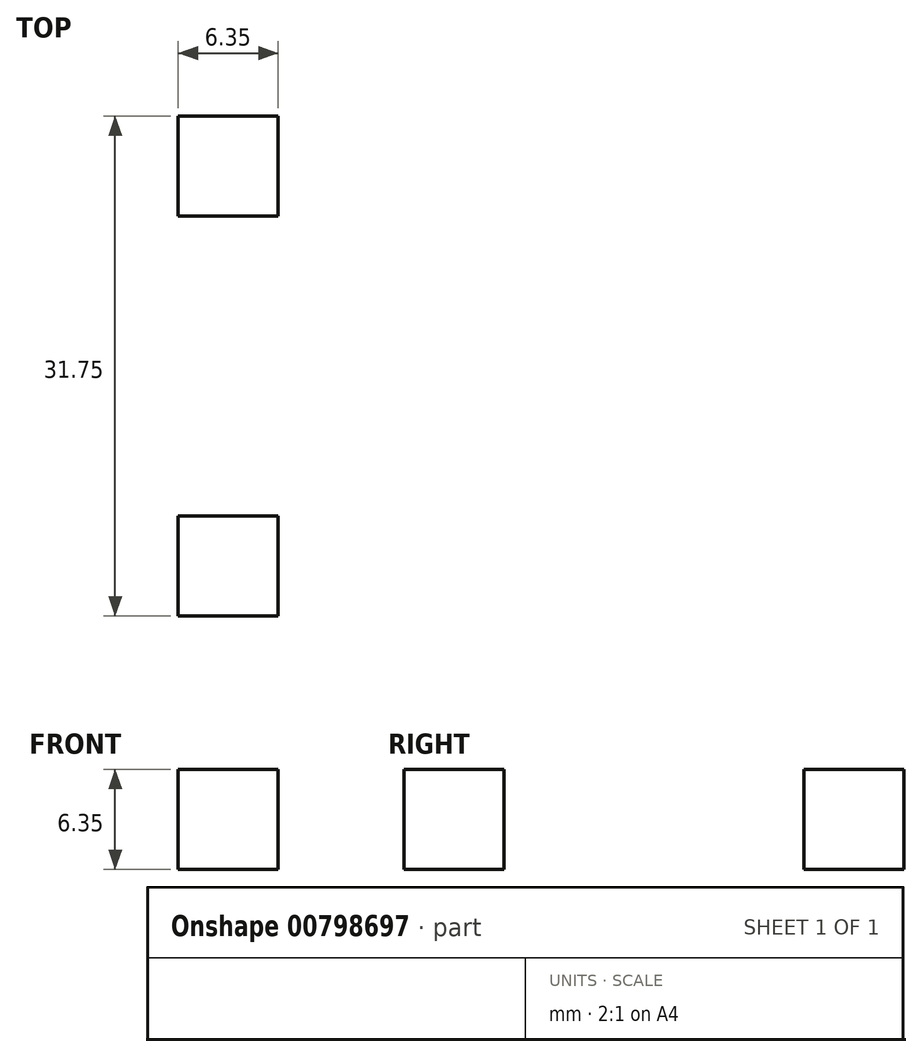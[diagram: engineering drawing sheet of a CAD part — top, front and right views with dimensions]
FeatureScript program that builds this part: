
annotation { "Feature Type Name" : "Feature", "Feature Type Description" : "" }
export const myFeature = defineFeature(function(context is Context, id is Id, definition is map)
    precondition{}
    {
        {
            var Q0;
            Q0=qCreatedBy(makeId("Top.planeOp"),FACE);
            var sketch = newSketch(context, id + "F0", { "sketchPlane" : qUnion([Q0])});
            skLineSegment(sketch, "E0.bottom", {"start": v(0, 0) * mm, "end": v(225.43, 0) * mm});
            skLineSegment(sketch, "E0.top", {"start": v(0, 31.75) * mm, "end": v(225.43, 31.75) * mm});
            skLineSegment(sketch, "E0.left", {"start": v(0, 0) * mm, "end": v(0, 31.75) * mm});
            skLineSegment(sketch, "E0.right", {"start": v(225.43, 0) * mm, "end": v(225.43, 31.75) * mm});
            skLineSegment(sketch, "E1.bottom", {"start": v(0, 31.75) * mm, "end": v(6.35, 31.75) * mm});
            skLineSegment(sketch, "E1.top", {"start": v(0, 25.4) * mm, "end": v(6.35, 25.4) * mm});
            skLineSegment(sketch, "E1.left", {"start": v(0, 31.75) * mm, "end": v(0, 25.4) * mm});
            skLineSegment(sketch, "E1.right", {"start": v(6.35, 31.75) * mm, "end": v(6.35, 25.4) * mm});
            skLineSegment(sketch, "E2.bottom", {"start": v(0, 0) * mm, "end": v(6.35, 0) * mm});
            skLineSegment(sketch, "E2.top", {"start": v(0, 6.35) * mm, "end": v(6.35, 6.35) * mm});
            skLineSegment(sketch, "E2.left", {"start": v(0, 0) * mm, "end": v(0, 6.35) * mm});
            skLineSegment(sketch, "E2.right", {"start": v(6.35, 0) * mm, "end": v(6.35, 6.35) * mm});
            skLineSegment(sketch, "E3.bottom", {"start": v(31.75, 0) * mm, "end": v(38.1, 0) * mm});
            skLineSegment(sketch, "E3.top", {"start": v(31.75, 6.35) * mm, "end": v(38.1, 6.35) * mm});
            skLineSegment(sketch, "E3.left", {"start": v(31.75, 0) * mm, "end": v(31.75, 6.35) * mm});
            skLineSegment(sketch, "E3.right", {"start": v(38.1, 0) * mm, "end": v(38.1, 6.35) * mm});
            skLineSegment(sketch, "E4.bottom", {"start": v(31.75, 25.4) * mm, "end": v(38.1, 25.4) * mm});
            skLineSegment(sketch, "E4.top", {"start": v(31.75, 31.75) * mm, "end": v(38.1, 31.75) * mm});
            skLineSegment(sketch, "E4.left", {"start": v(31.75, 25.4) * mm, "end": v(31.75, 31.75) * mm});
            skLineSegment(sketch, "E4.right", {"start": v(38.1, 25.4) * mm, "end": v(38.1, 31.75) * mm});
            skLineSegment(sketch, "E5.bottom", {"start": v(219.08, 6.35) * mm, "end": v(225.43, 6.35) * mm});
            skLineSegment(sketch, "E5.top", {"start": v(219.08, 0) * mm, "end": v(225.43, 0) * mm});
            skLineSegment(sketch, "E5.left", {"start": v(219.08, 6.35) * mm, "end": v(219.08, 0) * mm});
            skLineSegment(sketch, "E5.right", {"start": v(225.43, 6.35) * mm, "end": v(225.43, 0) * mm});
            skLineSegment(sketch, "E6.bottom", {"start": v(219.08, 25.4) * mm, "end": v(225.43, 25.4) * mm});
            skLineSegment(sketch, "E6.top", {"start": v(219.08, 31.75) * mm, "end": v(225.43, 31.75) * mm});
            skLineSegment(sketch, "E6.left", {"start": v(219.08, 25.4) * mm, "end": v(219.08, 31.75) * mm});
            skLineSegment(sketch, "E6.right", {"start": v(225.43, 25.4) * mm, "end": v(225.43, 31.75) * mm});
            skLineSegment(sketch, "E7.bottom", {"start": v(193.68, 6.35) * mm, "end": v(187.33, 6.35) * mm});
            skLineSegment(sketch, "E7.top", {"start": v(193.68, 0) * mm, "end": v(187.33, 0) * mm});
            skLineSegment(sketch, "E7.left", {"start": v(193.68, 6.35) * mm, "end": v(193.68, 0) * mm});
            skLineSegment(sketch, "E7.right", {"start": v(187.33, 6.35) * mm, "end": v(187.33, 0) * mm});
            skLineSegment(sketch, "E8.bottom", {"start": v(193.68, 25.4) * mm, "end": v(187.33, 25.4) * mm});
            skLineSegment(sketch, "E8.top", {"start": v(193.68, 31.75) * mm, "end": v(187.33, 31.75) * mm});
            skLineSegment(sketch, "E8.left", {"start": v(193.68, 25.4) * mm, "end": v(193.68, 31.75) * mm});
            skLineSegment(sketch, "E8.right", {"start": v(187.33, 25.4) * mm, "end": v(187.33, 31.75) * mm});
            skSolve(sketch);
        }
        {
            var Q0;
            Q0=makeQuery(id+"F0.imprint","IMPRINT",FACE,{"disambiguationData":[TD([[makeQuery(id+"F0.imprint","IMPRINT",EDGE,{"derivedFrom":sQuery(id+"F0.wireOp",EDGE,"E0.left")}),-1.0]])]});
            extrude(context, id + "F1", {"entities" : qUnion([Q0]), "depth" : 6.35 * mm, "offsetDistance" : 25.4 * mm});
        }
    });
